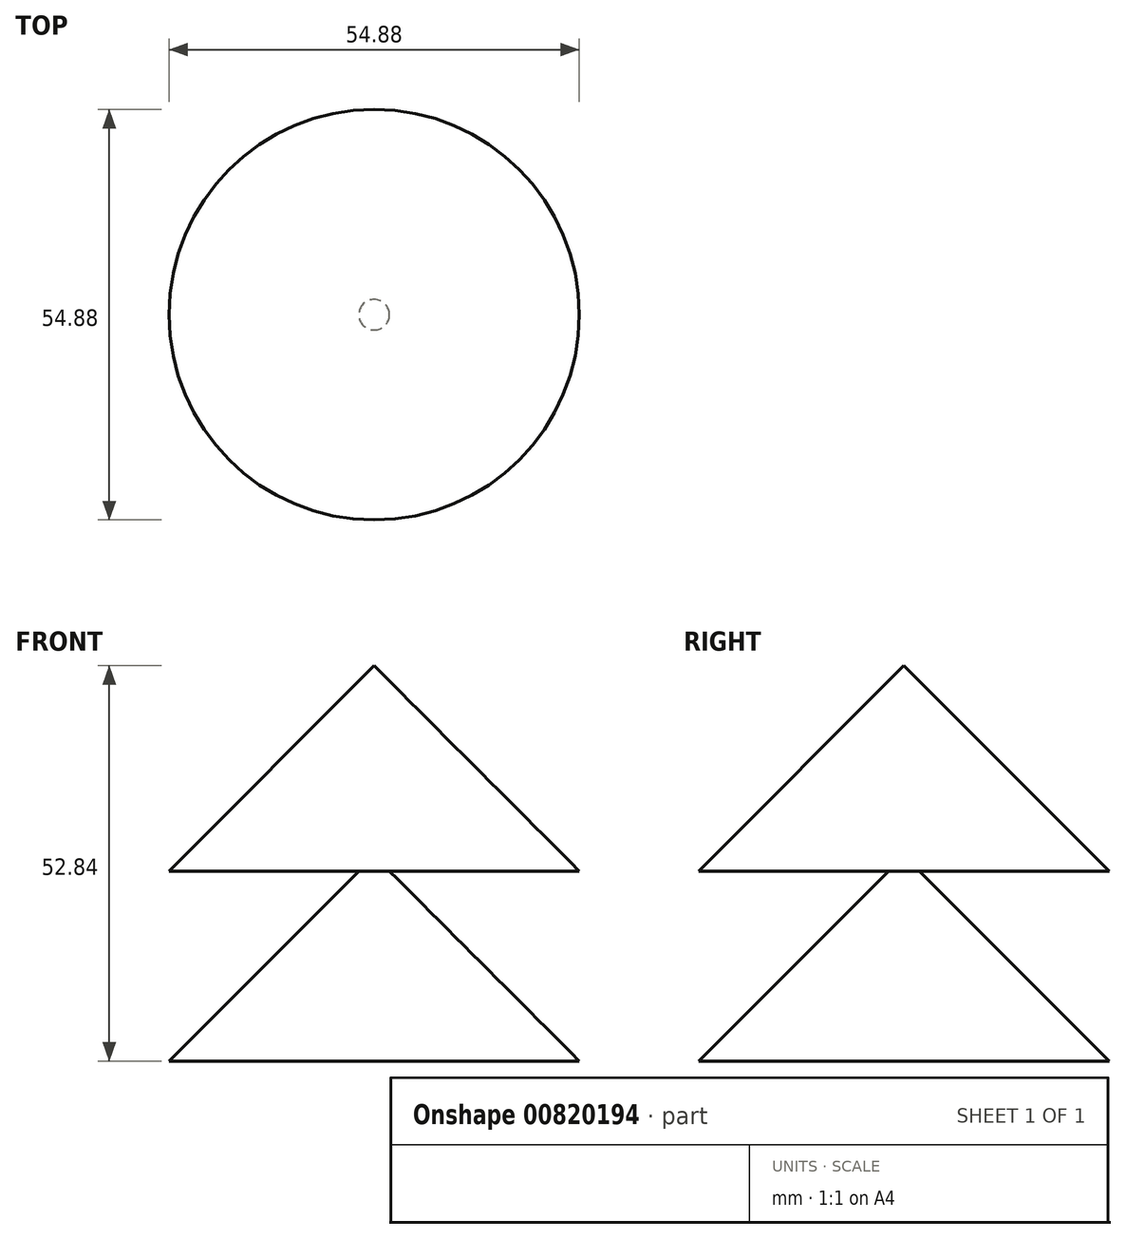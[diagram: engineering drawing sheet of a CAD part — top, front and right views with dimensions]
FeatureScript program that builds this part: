
annotation { "Feature Type Name" : "Feature", "Feature Type Description" : "" }
export const myFeature = defineFeature(function(context is Context, id is Id, definition is map)
    precondition{}
    {
        {
            var Q0;
            Q0=qCreatedBy(makeId("Top.planeOp"),FACE);
            var sketch = newSketch(context, id + "F0", { "sketchPlane" : qUnion([Q0])});
            skCircle(sketch, "E0", {"center": v(0, 0) * mm, "radius": 27.44 * mm});
            skSolve(sketch);
        }
        {
            var Q0;
            Q0=makeQuery(id+"F0.imprint","IMPRINT",FACE,{"disambiguationData":[TD([[makeQuery(id+"F0.imprint","IMPRINT",EDGE,{"derivedFrom":sQuery(id+"F0.wireOp",EDGE,"E0")}),1.0]])]});
            extrude(context, id + "F1", {"entities" : qUnion([Q0]), "depth" : 30 * mm, "offsetDistance" : 25.4 * mm, "hasDraft" : true, "draftAngle" : 45 * degree, "draftPullDirection" : true});
        }
        {
            var Q0;
            Q0=qCreatedBy(makeId("Top.planeOp"),FACE);
            cPlane(context, id + "F2", {"entities" : qUnion([Q0]), "cplaneType" : CPlaneType.OFFSET, "offset" : 25.4 * mm, "width" : 152.4 * mm, "height" : 152.4 * mm});
        }
        {
            var Q0;
            Q0=qCreatedBy(id+"F2.planeOp",FACE);
            var sketch = newSketch(context, id + "F3", { "sketchPlane" : qUnion([Q0])});
            skCircle(sketch, "E1.0", {"center": v(0, 0) * mm, "radius": 27.44 * mm});
            skSolve(sketch);
        }
        {
            var Q0;
            Q0=makeQuery(id+"F3.imprint","IMPRINT",FACE,{"disambiguationData":[TD([[makeQuery(id+"F3.imprint","IMPRINT",EDGE,{"derivedFrom":sQuery(id+"F3.wireOp",EDGE,"E1.0")}),1.0]])]});
            extrude(context, id + "F4", {"entities" : qUnion([Q0]), "operationType" : NewBodyOperationType.ADD, "depth" : 30 * mm, "offsetDistance" : 25.4 * mm, "hasDraft" : true, "draftAngle" : 45 * degree, "draftPullDirection" : true});
        }
    });
